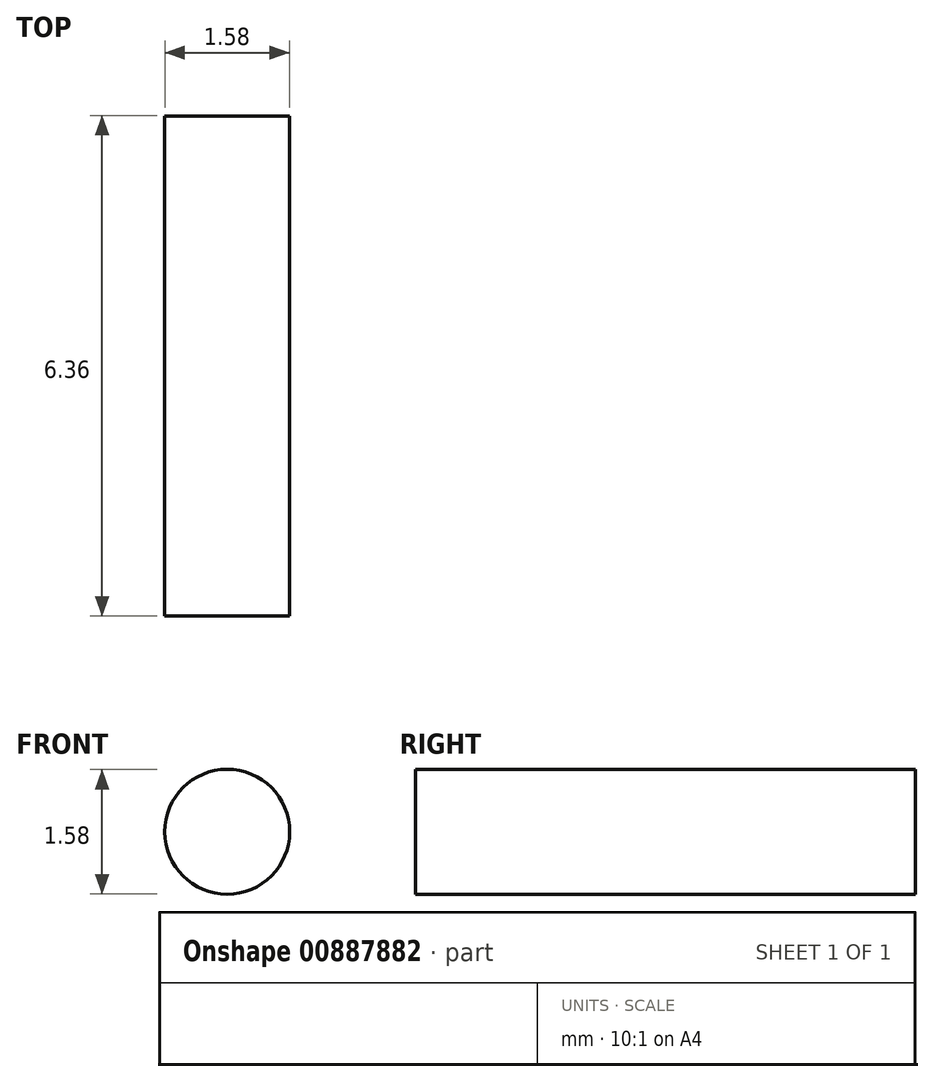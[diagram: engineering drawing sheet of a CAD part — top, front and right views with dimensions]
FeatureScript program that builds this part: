
annotation { "Feature Type Name" : "Feature", "Feature Type Description" : "" }
export const myFeature = defineFeature(function(context is Context, id is Id, definition is map)
    precondition{}
    {
        {
            var Q0;
            Q0=qCreatedBy(makeId("Front.planeOp"),FACE);
            var sketch = newSketch(context, id + "F0", { "sketchPlane" : qUnion([Q0])});
            skCircle(sketch, "E0", {"center": v(0, 0) * mm, "radius": 0.8 * mm});
            skSolve(sketch);
        }
        {
            var Q0;
            Q0=makeQuery(id+"F0.imprint","IMPRINT",FACE,{"disambiguationData":[TD([[makeQuery(id+"F0.imprint","IMPRINT",EDGE,{"derivedFrom":sQuery(id+"F0.wireOp",EDGE,"E0")}),1.0]])]});
            extrude(context, id + "F1", {"entities" : qUnion([Q0]), "depth" : 6.35 * mm, "offsetDistance" : 25.4 * mm, "symmetric" : true});
        }
        {
            var Q0;
            Q0=makeQuery(id+"F1.opExtrude","SWEPT_BODY",BODY,{"disambiguationData":[OSD([sQuery(id+"F0.wireOp",EDGE,"E0")])]});
            transform(context, id + "F2", {"entities" : qUnion([Q0]), "transformType" : TransformType.COPY});
        }
    });
